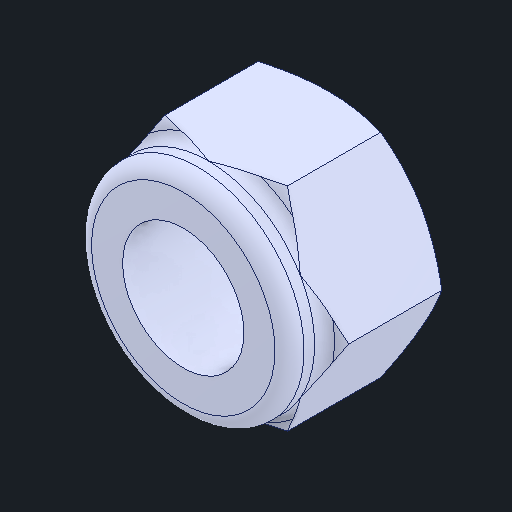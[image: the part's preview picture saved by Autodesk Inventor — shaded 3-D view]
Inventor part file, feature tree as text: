
AUTODESK INVENTOR PART (.ipt)
format: ipt  version: 2024 (Build 280153000, 153)  size: 177,664 bytes
history: native  units: in
note: dims shown in document units (in); Inventor stores cm internally (conversion verified against a paired STEP export)
features: fillet x1
ambient origin geometry x8: Origin, YZ Plane, XZ Plane, XY Plane, X Axis, Y Axis, Z Axis, Center Point
bodies: Solid1 (feature_tree)
feature tree (1):
  fillet  "Fillet7"  [1 undecoded]
note: 1 required parameter value undecoded (feature->parameter linkage not recoverable at this tier; creation-order binding heuristic only, values carry confidence <= 0.55)
